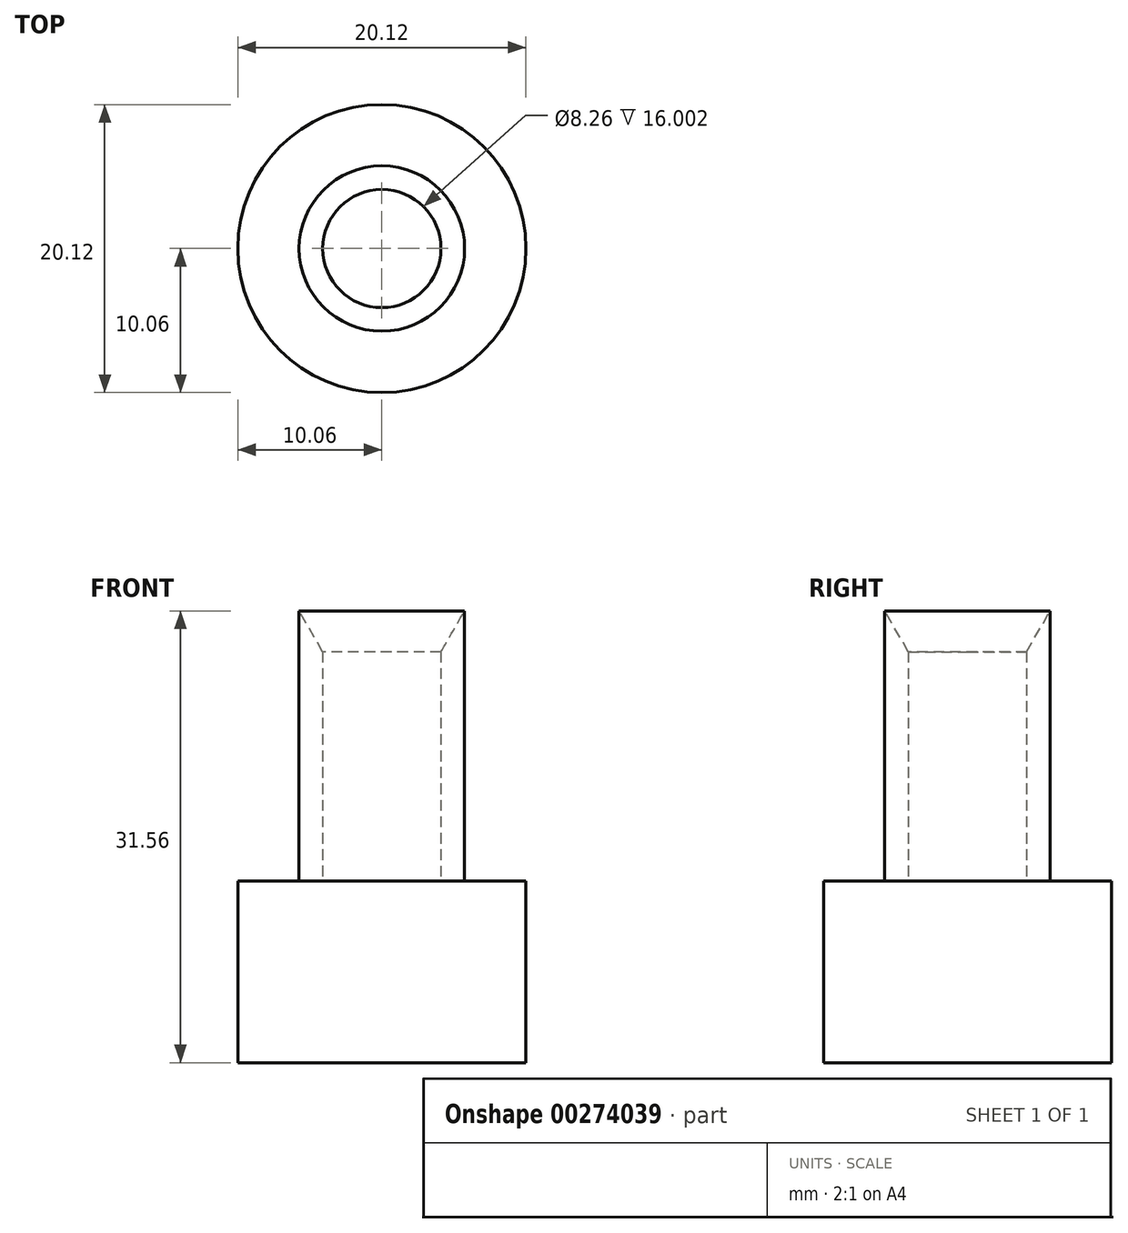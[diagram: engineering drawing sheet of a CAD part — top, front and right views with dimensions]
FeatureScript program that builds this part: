
annotation { "Feature Type Name" : "Feature", "Feature Type Description" : "" }
export const myFeature = defineFeature(function(context is Context, id is Id, definition is map)
    precondition{}
    {
        {
            var Q0;
            Q0=qCreatedBy(makeId("Top.planeOp"),FACE);
            var sketch = newSketch(context, id + "F0", { "sketchPlane" : qUnion([Q0])});
            skCircle(sketch, "E0", {"center": v(0, 0) * mm, "radius": 10.06 * mm});
            skSolve(sketch);
        }
        {
            var Q0;
            Q0=makeQuery(id+"F0.imprint","IMPRINT",FACE,{"disambiguationData":[TD([[makeQuery(id+"F0.imprint","IMPRINT",EDGE,{"derivedFrom":sQuery(id+"F0.wireOp",EDGE,"E0")}),1.0]])]});
            extrude(context, id + "F1", {"entities" : qUnion([Q0]), "depth" : 12.7 * mm});
        }
        {
            var Q0;
            Q0=makeQuery(id+"F1.opExtrude","CAP_FACE",FACE,{"disambiguationData":[OSD([sQuery(id+"F0.wireOp",EDGE,"E0")])],"isStart":false});
            var sketch = newSketch(context, id + "F2", { "sketchPlane" : qUnion([Q0])});
            skCircle(sketch, "E1", {"center": v(0, 0) * mm, "radius": 5.78 * mm});
            skCircle(sketch, "E2", {"center": v(0, 0) * mm, "radius": 4.13 * mm});
            skSolve(sketch);
        }
        {
            var Q0;
            Q0 = qSketchRegion(id + "F2", true);
            extrude(context, id + "F3", {"entities" : qUnion([Q0]), "operationType" : NewBodyOperationType.ADD, "depth" : 19.05 * mm});
        }
        {
            var Q0;
            Q0=makeQuery(id+"F3.opExtrude","CAP_EDGE",EDGE,{"disambiguationData":[OSD([sQuery(id+"F2.wireOp",EDGE,"E2")])],"isStart":false});
            chamfer(context, id + "F4", {"entities" : qUnion([Q0]), "chamferType" : ChamferType.OFFSET_ANGLE, "width" : 3.05 * mm, "oppositeDirection" : false, "angle" : 30 * degree, "tangentPropagation" : true});
        }
    });
